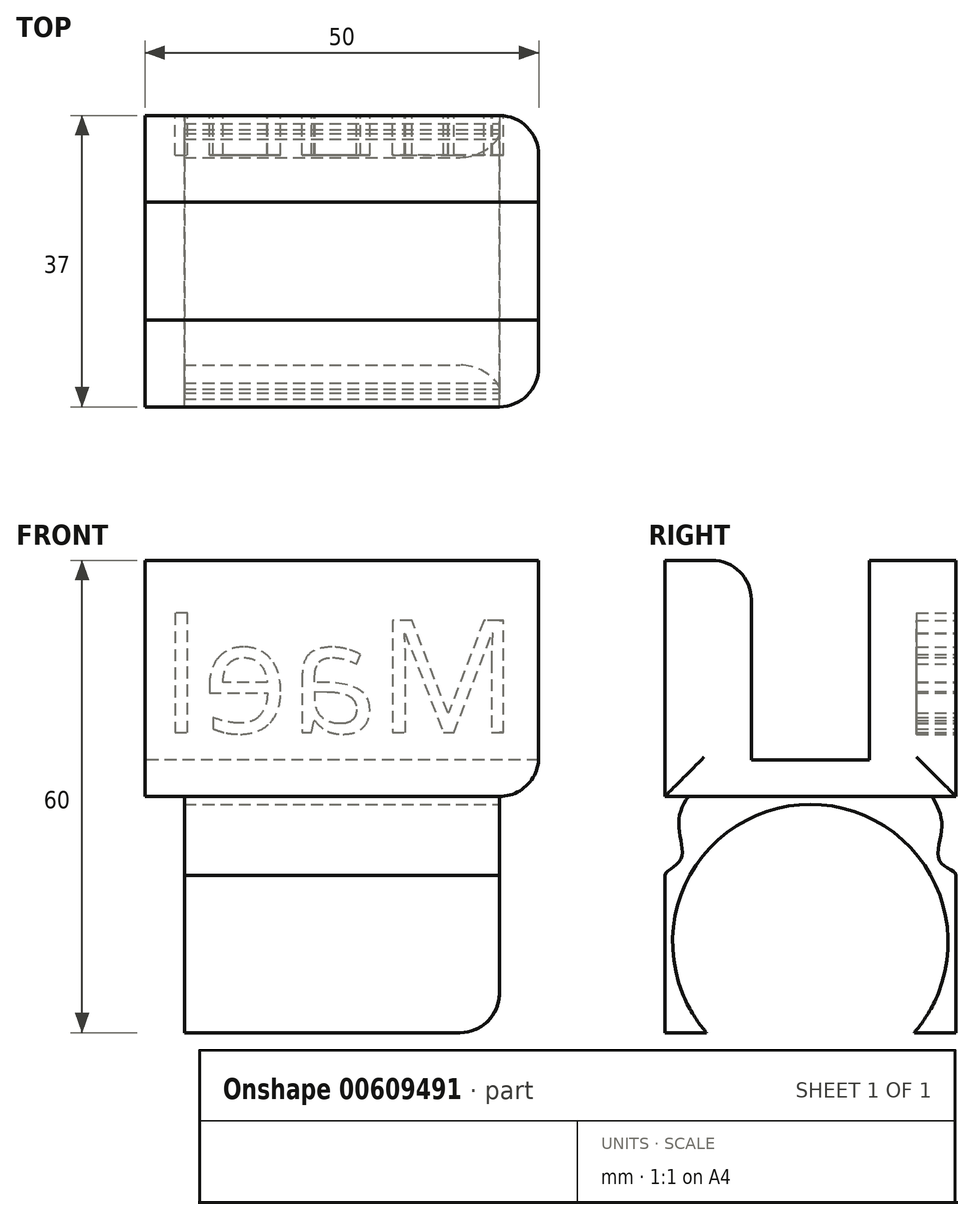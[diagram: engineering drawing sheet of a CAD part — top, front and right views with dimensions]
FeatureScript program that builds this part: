
annotation { "Feature Type Name" : "Feature", "Feature Type Description" : "" }
export const myFeature = defineFeature(function(context is Context, id is Id, definition is map)
    precondition{}
    {
        {
            var Q0;
            Q0=qCreatedBy(makeId("Front.planeOp"),FACE);
            var sketch = newSketch(context, id + "F0", { "sketchPlane" : qUnion([Q0])});
            skLineSegment(sketch, "E0.bottom", {"start": v(-24.12, 16) * mm, "end": v(25.88, 16) * mm});
            skLineSegment(sketch, "E0.top", {"start": v(-24.12, -14) * mm, "end": v(25.88, -14) * mm});
            skLineSegment(sketch, "E0.left", {"start": v(-24.12, 16) * mm, "end": v(-24.12, -14) * mm});
            skLineSegment(sketch, "E0.right", {"start": v(25.88, 16) * mm, "end": v(25.88, -14) * mm});
            skSolve(sketch);
        }
        {
            var Q0;
            Q0 = qSketchRegion(id + "F0", true);
            extrude(context, id + "F1", {"entities" : qUnion([Q0]), "depth" : 53 * mm, "offsetDistance" : 25 * mm});
        }
        {
            var Q0;
            Q0=makeQuery(id+"F1.opExtrude","SWEPT_FACE",FACE,{"disambiguationData":[OSD([sQuery(id+"F0.wireOp",EDGE,"E0.left")])]});
            var sketch = newSketch(context, id + "F2", { "sketchPlane" : qUnion([Q0])});
            skLineSegment(sketch, "E1.top", {"start": v(5, -14) * mm, "end": v(35, -14) * mm});
            skLineSegment(sketch, "E2.bottom", {"start": v(19, 16) * mm, "end": v(34, 16) * mm});
            skLineSegment(sketch, "E2.top", {"start": v(19, -9.34) * mm, "end": v(34, -9.34) * mm});
            skLineSegment(sketch, "E2.left", {"start": v(19, 16) * mm, "end": v(19, -9.34) * mm});
            skLineSegment(sketch, "E2.right", {"start": v(34, 16) * mm, "end": v(34, -9.34) * mm});
            skSolve(sketch);
        }
        {
            var Q0;
            Q0 = qSketchRegion(id + "F2", true);
            extrude(context, id + "F3", {"entities" : qUnion([Q0]), "operationType" : NewBodyOperationType.REMOVE, "endBound" : BoundingType.THROUGH_ALL, "oppositeDirection" : true, "depth" : 25 * mm, "offsetDistance" : 25 * mm});
        }
        {
            var Q0;
            Q0=makeQuery(id+"F1.opExtrude","SWEPT_FACE",FACE,{"disambiguationData":[OSD([sQuery(id+"F0.wireOp",EDGE,"E0.top")])]});
            var sketch = newSketch(context, id + "F4", { "sketchPlane" : qUnion([Q0])});
            skLineSegment(sketch, "E3.bottom", {"start": v(-19.12, 49) * mm, "end": v(20.88, 49) * mm});
            skLineSegment(sketch, "E3.top", {"start": v(-19.12, 4) * mm, "end": v(20.88, 4) * mm});
            skLineSegment(sketch, "E3.left", {"start": v(-19.12, 49) * mm, "end": v(-19.12, 4) * mm});
            skLineSegment(sketch, "E3.right", {"start": v(20.88, 49) * mm, "end": v(20.88, 4) * mm});
            skSolve(sketch);
        }
        {
            var Q0;
            Q0 = qSketchRegion(id + "F4", true);
            extrude(context, id + "F5", {"entities" : qUnion([Q0]), "operationType" : NewBodyOperationType.ADD, "depth" : 10 * mm, "offsetDistance" : 25 * mm});
        }
        {
            var Q0;
            Q0=makeQuery(id+"F5.opExtrude","SWEPT_FACE",FACE,{"disambiguationData":[OSD([sQuery(id+"F4.wireOp",EDGE,"E3.right")])]});
            var sketch = newSketch(context, id + "F6", { "sketchPlane" : qUnion([Q0])});
            skFitSpline(sketch, "E4", {"points": [v(-8, -24) * mm, v(-10, -22.35) * mm, v(-9.8, -17.8) * mm, v(-11, -14) * mm], "startDerivative": vector(0.68, 5.98) * mm, "endDerivative": vector(-4.77, 9.53) * mm});
            skFitSpline(sketch, "E5", {"points": [v(-45, -24) * mm, v(-43, -22.07) * mm, v(-43.2, -18.08) * mm, v(-42, -14) * mm], "startDerivative": vector(1.97, 6.9) * mm, "endDerivative": vector(7.56, 10.02) * mm});
            skSolve(sketch);
        }
        {
            var Q0;
            Q0 = qSketchRegion(id + "F6", true);
            var Q1;
            {var subQ0=sQuery(id+"F6.wireOp",EDGE,"E4");Q1=makeQuery(id+"F6.imprint","IMPRINT",FACE,{"disambiguationData":[TD([[makeQuery(id+"F6.imprint","IMPRINT",EDGE,{"derivedFrom":subQ0}),-1.0]])]});}
            var Q2;
            {var subQ0=sQuery(id+"F6.wireOp",EDGE,"E5");Q2=makeQuery(id+"F6.imprint","IMPRINT",FACE,{"disambiguationData":[TD([[makeQuery(id+"F6.imprint","IMPRINT",EDGE,{"derivedFrom":subQ0}),1.0]])]});}
            extrude(context, id + "F7", {"entities" : qUnion([Q0, Q1, Q2]), "operationType" : NewBodyOperationType.REMOVE, "endBound" : BoundingType.THROUGH_ALL, "oppositeDirection" : true, "depth" : 25 * mm, "offsetDistance" : 25 * mm});
        }
        {
            var Q0;
            Q0=makeQuery(id+"F5.opExtrude","CAP_FACE",FACE,{"disambiguationData":[OSD([sQuery(id+"F4.wireOp",EDGE,"E3.bottom"),sQuery(id+"F4.wireOp",EDGE,"E3.top"),sQuery(id+"F4.wireOp",EDGE,"E3.left"),sQuery(id+"F4.wireOp",EDGE,"E3.right")])],"isStart":false});
            extrude(context, id + "F8", {"entities" : qUnion([Q0]), "operationType" : NewBodyOperationType.ADD, "depth" : 20 * mm, "offsetDistance" : 25 * mm});
        }
        {
            var Q0;
            {var subQ0=sQuery(id+"F4.wireOp",EDGE,"E3.right");Q0=makeQuery(id+"F8.boolean.opBoolean","MERGE",FACE,{"derivedFrom":[makeQuery(id+"F5.opExtrude","SWEPT_FACE",FACE,{"disambiguationData":[OSD([subQ0])]}),makeQuery(id+"F8.opExtrude","SWEPT_FACE",FACE,{"disambiguationData":[OSD([subQ0])]})]});}
            var sketch = newSketch(context, id + "F9", { "sketchPlane" : qUnion([Q0])});
            skCircle(sketch, "E6", {"center": v(-26.5, -32.5) * mm, "radius": 17.5 * mm});
            skSolve(sketch);
        }
        {
            var Q0;
            Q0 = qSketchRegion(id + "F9", true);
            extrude(context, id + "F10", {"entities" : qUnion([Q0]), "operationType" : NewBodyOperationType.REMOVE, "endBound" : BoundingType.THROUGH_ALL, "oppositeDirection" : true, "depth" : 25 * mm, "offsetDistance" : 25 * mm});
        }
        {
            var Q0;
            Q0=makeQuery(id+"F1.opExtrude","SWEPT_FACE",FACE,{"disambiguationData":[OSD([sQuery(id+"F0.wireOp",EDGE,"E0.left")])]});
            var sketch = newSketch(context, id + "F11", { "sketchPlane" : qUnion([Q0])});
            skLineSegment(sketch, "E7.bottom", {"start": v(0, 16) * mm, "end": v(8, 16) * mm});
            skLineSegment(sketch, "E7.top", {"start": v(0, -14) * mm, "end": v(8, -14) * mm});
            skLineSegment(sketch, "E7.left", {"start": v(0, 16) * mm, "end": v(0, -14) * mm});
            skLineSegment(sketch, "E7.right", {"start": v(8, 16) * mm, "end": v(8, -14) * mm});
            skLineSegment(sketch, "E8.bottom", {"start": v(53, 16) * mm, "end": v(45, 16) * mm});
            skLineSegment(sketch, "E8.top", {"start": v(53, -14) * mm, "end": v(45, -14) * mm});
            skLineSegment(sketch, "E8.left", {"start": v(53, 16) * mm, "end": v(53, -14) * mm});
            skLineSegment(sketch, "E8.right", {"start": v(45, 16) * mm, "end": v(45, -14) * mm});
            skSolve(sketch);
        }
        {
            var Q0;
            Q0 = qSketchRegion(id + "F11", true);
            extrude(context, id + "F12", {"entities" : qUnion([Q0]), "operationType" : NewBodyOperationType.REMOVE, "endBound" : BoundingType.THROUGH_ALL, "oppositeDirection" : true, "depth" : 25 * mm, "offsetDistance" : 25 * mm});
        }
        {
            var Q0;
            Q0=makeQuery(id+"F12.boolean.opBoolean","COPY",FACE,{"derivedFrom":makeQuery(id+"F12.opExtrude","SWEPT_FACE",FACE,{"disambiguationData":[OSD([sQuery(id+"F11.wireOp",EDGE,"E7.right")])]})});
            var sketch = newSketch(context, id + "F13", { "sketchPlane" : qUnion([Q0])});
            skText(sketch, "E9", { "text": "Mael\n", "fontName": "OpenSans-Regular.ttf"});
            const initialGuessF13  = {"E9": [-0.02338, -0.0059, 1, 0, 0.01439]};
            skSetInitialGuess(sketch, initialGuessF13);
            skSolve(sketch);
        }
        {
            var Q0;
            Q0 = qSketchRegion(id + "F13", true);
            extrude(context, id + "F14", {"entities" : qUnion([Q0]), "operationType" : NewBodyOperationType.REMOVE, "oppositeDirection" : true, "depth" : 5 * mm, "offsetDistance" : 25 * mm});
        }
        {
            var Q0;
            Q0=makeQuery(id+"F12.boolean.opBoolean","COPY",EDGE,{"derivedFrom":makeQuery(id+"F12.opExtrude","SWEPT_EDGE",EDGE,{"disambiguationData":[OSD([sQuery(id+"F0.wireOp",EDGE,"E0.bottom"),sQuery(id+"F0.wireOp",EDGE,"E0.left"),sQuery(id+"F11.wireOp",EDGE,"E7.bottom"),sQuery(id+"F11.wireOp",EDGE,"E7.right")])]})});
            var Q1;
            Q1=makeQuery(id+"F12.boolean.opBoolean","INTERSECT",EDGE,{"derivedFrom":[makeQuery(id+"F1.opExtrude","SWEPT_FACE",FACE,{"disambiguationData":[OSD([sQuery(id+"F0.wireOp",EDGE,"E0.right")])]}),makeQuery(id+"F12.opExtrude","SWEPT_FACE",FACE,{"disambiguationData":[OSD([sQuery(id+"F11.wireOp",EDGE,"E7.right")])]})]});
            var Q2;
            Q2=makeQuery(id+"F12.boolean.opBoolean","COPY",EDGE,{"derivedFrom":makeQuery(id+"F12.opExtrude","CAP_EDGE",EDGE,{"disambiguationData":[OSD([sQuery(id+"F11.wireOp",EDGE,"E7.right")])],"isStart":true})});
            var Q3;
            Q3=makeQuery(id+"F12.boolean.opBoolean","COPY",EDGE,{"derivedFrom":makeQuery(id+"F12.opExtrude","CAP_EDGE",EDGE,{"disambiguationData":[OSD([sQuery(id+"F11.wireOp",EDGE,"E8.right")])],"isStart":true})});
            var Q4;
            Q4=makeQuery(id+"F12.boolean.opBoolean","COPY",EDGE,{"derivedFrom":makeQuery(id+"F12.opExtrude","SWEPT_EDGE",EDGE,{"disambiguationData":[OSD([sQuery(id+"F0.wireOp",EDGE,"E0.bottom"),sQuery(id+"F0.wireOp",EDGE,"E0.left"),sQuery(id+"F11.wireOp",EDGE,"E8.bottom"),sQuery(id+"F11.wireOp",EDGE,"E8.right")])]})});
            var Q5;
            Q5=makeQuery(id+"F12.boolean.opBoolean","INTERSECT",EDGE,{"derivedFrom":[makeQuery(id+"F1.opExtrude","SWEPT_FACE",FACE,{"disambiguationData":[OSD([sQuery(id+"F0.wireOp",EDGE,"E0.right")])]}),makeQuery(id+"F12.opExtrude","SWEPT_FACE",FACE,{"disambiguationData":[OSD([sQuery(id+"F11.wireOp",EDGE,"E8.right")])]})]});
            var Q6;
            Q6=makeQuery(id+"F1.opExtrude","SWEPT_EDGE",EDGE,{"disambiguationData":[OSD([sQuery(id+"F0.wireOp",EDGE,"E0.top"),sQuery(id+"F0.wireOp",EDGE,"E0.right")])]});
            var Q7;
            {var subQ0=sQuery(id+"F4.wireOp",EDGE,"E3.right");var subQ1=makeQuery(id+"F5.opExtrude","CAP_EDGE",EDGE,{"disambiguationData":[OSD([subQ0])],"isStart":true});Q7=makeQuery(id+"F7.boolean.opBoolean","INTERSECT",EDGE,{"derivedFrom":[makeQuery(id+"F7.opExtrude","SWEPT_FACE",FACE,{"disambiguationData":[OSD([subQ0]),TDD([makeQuery(id+"F6.imprint","IMPRINT",EDGE,{"disambiguationData":[TD([[makeQuery(id+"F6.imprint","INTERSECT",VERTEX,{"derivedFrom":[subQ1,sQuery(id+"F6.wireOp",EDGE,"E5")]}),1.0]])],"derivedFrom":subQ1})])]}),makeQuery(id+"F7.opExtrude","SWEPT_FACE",FACE,{"disambiguationData":[OSD([subQ0]),TDD([makeQuery(id+"F6.imprint","IMPRINT",EDGE,{"disambiguationData":[TD([[makeQuery(id+"F6.imprint","INTERSECT",VERTEX,{"derivedFrom":[subQ1,sQuery(id+"F6.wireOp",EDGE,"E4")]}),-1.0]])],"derivedFrom":subQ1})])]})]});}
            var Q8;
            Q8=makeQuery(id+"F8.opExtrude","CAP_EDGE",EDGE,{"disambiguationData":[OSD([sQuery(id+"F4.wireOp",EDGE,"E3.right"),sQuery(id+"F6.wireOp",EDGE,"E4")])],"isStart":false});
            var Q9;
            Q9=makeQuery(id+"F8.opExtrude","CAP_EDGE",EDGE,{"disambiguationData":[OSD([sQuery(id+"F4.wireOp",EDGE,"E3.right"),sQuery(id+"F6.wireOp",EDGE,"E5")])],"isStart":false});
            var Q10;
            Q10=makeQuery(id+"F3.boolean.opBoolean","COPY",EDGE,{"derivedFrom":makeQuery(id+"F3.opExtrude","SWEPT_EDGE",EDGE,{"disambiguationData":[OSD([sQuery(id+"F0.wireOp",EDGE,"E0.bottom"),sQuery(id+"F0.wireOp",EDGE,"E0.left"),sQuery(id+"F2.wireOp",EDGE,"E2.bottom"),sQuery(id+"F2.wireOp",EDGE,"E2.left")])]})});
            var Q11;
            Q11=makeQuery(id+"F3.boolean.opBoolean","COPY",EDGE,{"derivedFrom":makeQuery(id+"F3.opExtrude","SWEPT_EDGE",EDGE,{"disambiguationData":[OSD([sQuery(id+"F0.wireOp",EDGE,"E0.bottom"),sQuery(id+"F0.wireOp",EDGE,"E0.left"),sQuery(id+"F2.wireOp",EDGE,"E2.bottom"),sQuery(id+"F2.wireOp",EDGE,"E2.right")])]})});
            fillet(context, id + "F15", {"entities" : qUnion([Q0, Q1, Q2, Q3, Q4, Q5, Q6, Q7, Q8, Q9, Q10, Q11]), "radius" : 5 * mm, "tangentPropagation" : true, "allowEdgeOverflow" : false});
        }
    });
